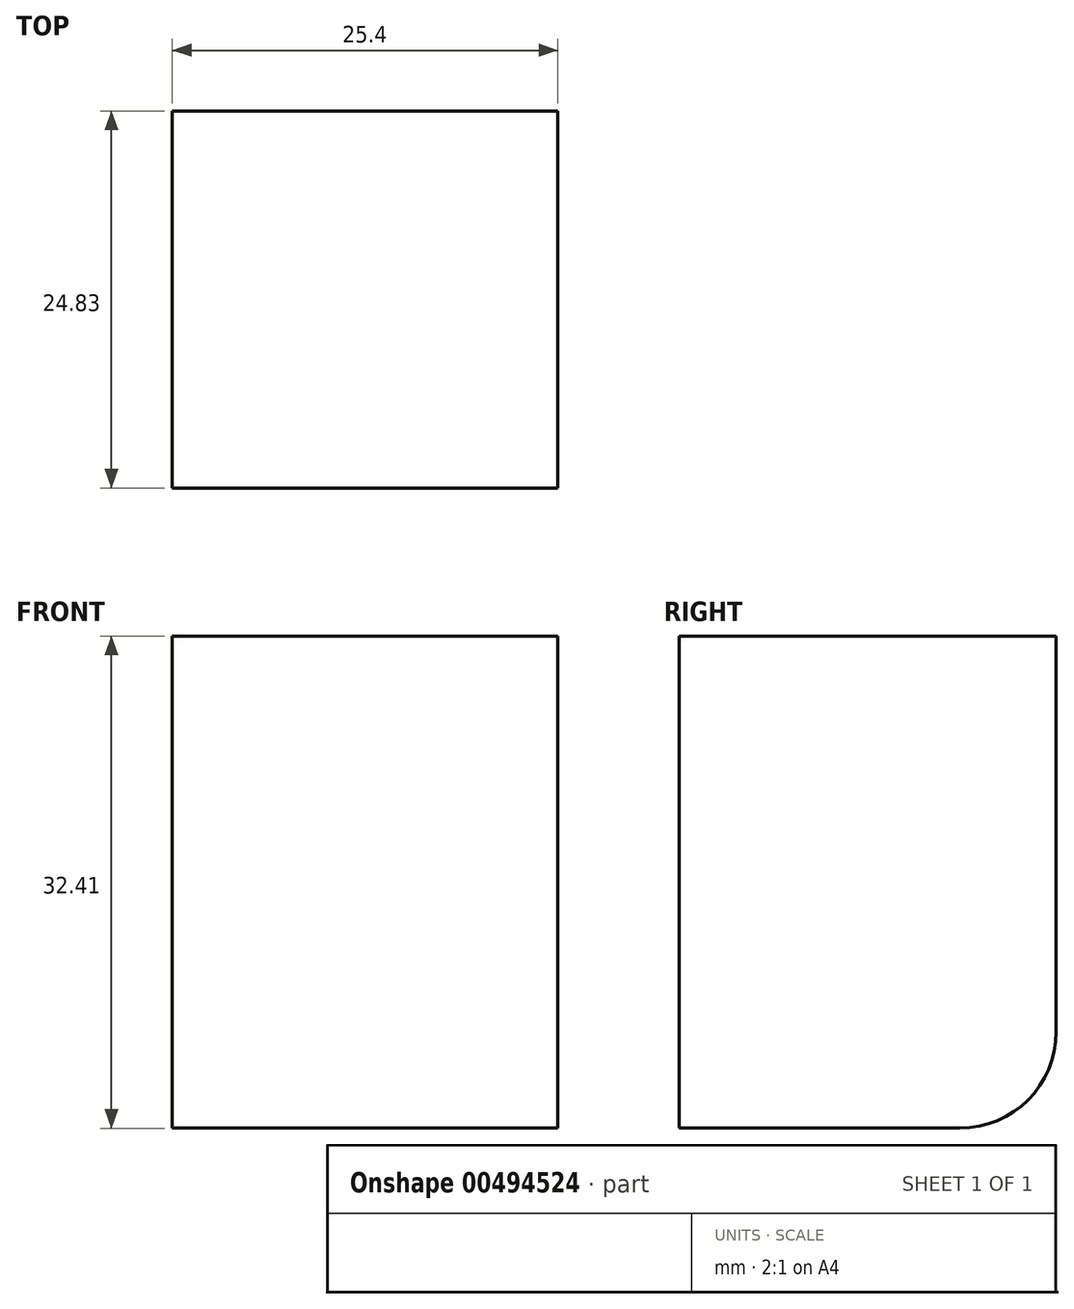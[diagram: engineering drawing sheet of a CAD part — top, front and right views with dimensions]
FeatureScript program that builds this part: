
annotation { "Feature Type Name" : "Feature", "Feature Type Description" : "" }
export const myFeature = defineFeature(function(context is Context, id is Id, definition is map)
    precondition{}
    {
        {
            var Q0;
            Q0=qCreatedBy(makeId("Right.planeOp"),FACE);
            var sketch = newSketch(context, id + "F0", { "sketchPlane" : qUnion([Q0])});
            skLineSegment(sketch, "E0.bottom", {"start": v(-35.62, 37.71) * mm, "end": v(-10.79, 37.71) * mm});
            skLineSegment(sketch, "E0.top", {"start": v(-35.62, 5.3) * mm, "end": v(-17.14, 5.3) * mm});
            skLineSegment(sketch, "E0.left", {"start": v(-35.62, 37.71) * mm, "end": v(-35.62, 5.3) * mm});
            skLineSegment(sketch, "E0.right", {"start": v(-10.79, 37.71) * mm, "end": v(-10.79, 11.65) * mm});
            skPoint(sketch, "E1.visualSharp", {"position": v(-10.79, 5.3) * mm});
            skArc(sketch, "E1.filletArc", {"start": v(-17.14, 5.3) * mm, "mid": v(-12.65, 7.16) * mm, "end": v(-10.79, 11.65) * mm});
            skLineSegment(sketch, "E2", {"start": v(-10.79, 37.71) * mm, "end": v(-10.79, 52.44) * mm});
            skLineSegment(sketch, "E3", {"start": v(-10.79, 52.44) * mm, "end": v(-35.62, 37.71) * mm});
            skSolve(sketch);
        }
        {
            var Q0;
            Q0=makeQuery(id+"F0.imprint","IMPRINT",FACE,{"disambiguationData":[TD([[makeQuery(id+"F0.imprint","IMPRINT",EDGE,{"derivedFrom":sQuery(id+"F0.wireOp",EDGE,"E0.bottom")}),-1.0]])]});
            extrude(context, id + "F1", {"entities" : qUnion([Q0]), "depth" : 25.4 * mm});
        }
    });
